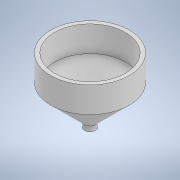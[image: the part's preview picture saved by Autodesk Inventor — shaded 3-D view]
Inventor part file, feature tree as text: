
AUTODESK INVENTOR PART (.ipt)
format: ipt  version: 2020 (Build 240168000, 168)  size: 119,296 bytes
history: native  units: mm
features: revolve x1, sketch x1
ambient origin geometry x8: Origin, YZ Plane, XZ Plane, XY Plane, X Axis, Y Axis, Z Axis, Center Point
bodies: Solid1 (feature_tree)
feature tree (2):
  revolve  "Revolution1"  [1 undecoded]
  sketch  "Sketch1"  dims[d0=50.0mm d1=30.5mm d2=20.0mm d3=90.0deg d4=37.0mm d5=135.0deg d6=3.0mm d7=90.0deg]
note: 1 required parameter value undecoded (feature->parameter linkage not recoverable at this tier; creation-order binding heuristic only, values carry confidence <= 0.55)
